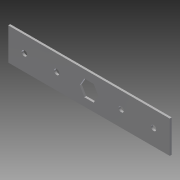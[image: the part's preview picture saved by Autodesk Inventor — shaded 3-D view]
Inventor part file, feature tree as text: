
AUTODESK INVENTOR PART (.ipt)
format: ipt  version: 2014 (Build 180170000, 170)  size: 94,208 bytes
history: native  units: in
note: dims shown in document units (in); Inventor stores cm internally (conversion verified against a paired STEP export)
features: extrude x1, sketch x1
ambient origin geometry x8: Origin, YZ Plane, XZ Plane, XY Plane, X Axis, Y Axis, Z Axis, Center Point
bodies: Solid1 (feature_tree)
feature tree (2):
  extrude  "Extrusion1"  Depth=1.0in
  sketch  "Sketch1"  dims[d0=5.0in d1=1.0in d4=0.5in d5=0.5in d6=2.5in d7=0.164in d8=0.164in d9=0.5in d10=0.5in d11=0.5in d12=0.5in d13=0.7874in d15=1.0in d16=0.3937in d18=1.0in d20=0.7874in d22=1.0in d23=0.3937in d25=1.0in d27=0.0625in d28=0.0in]
